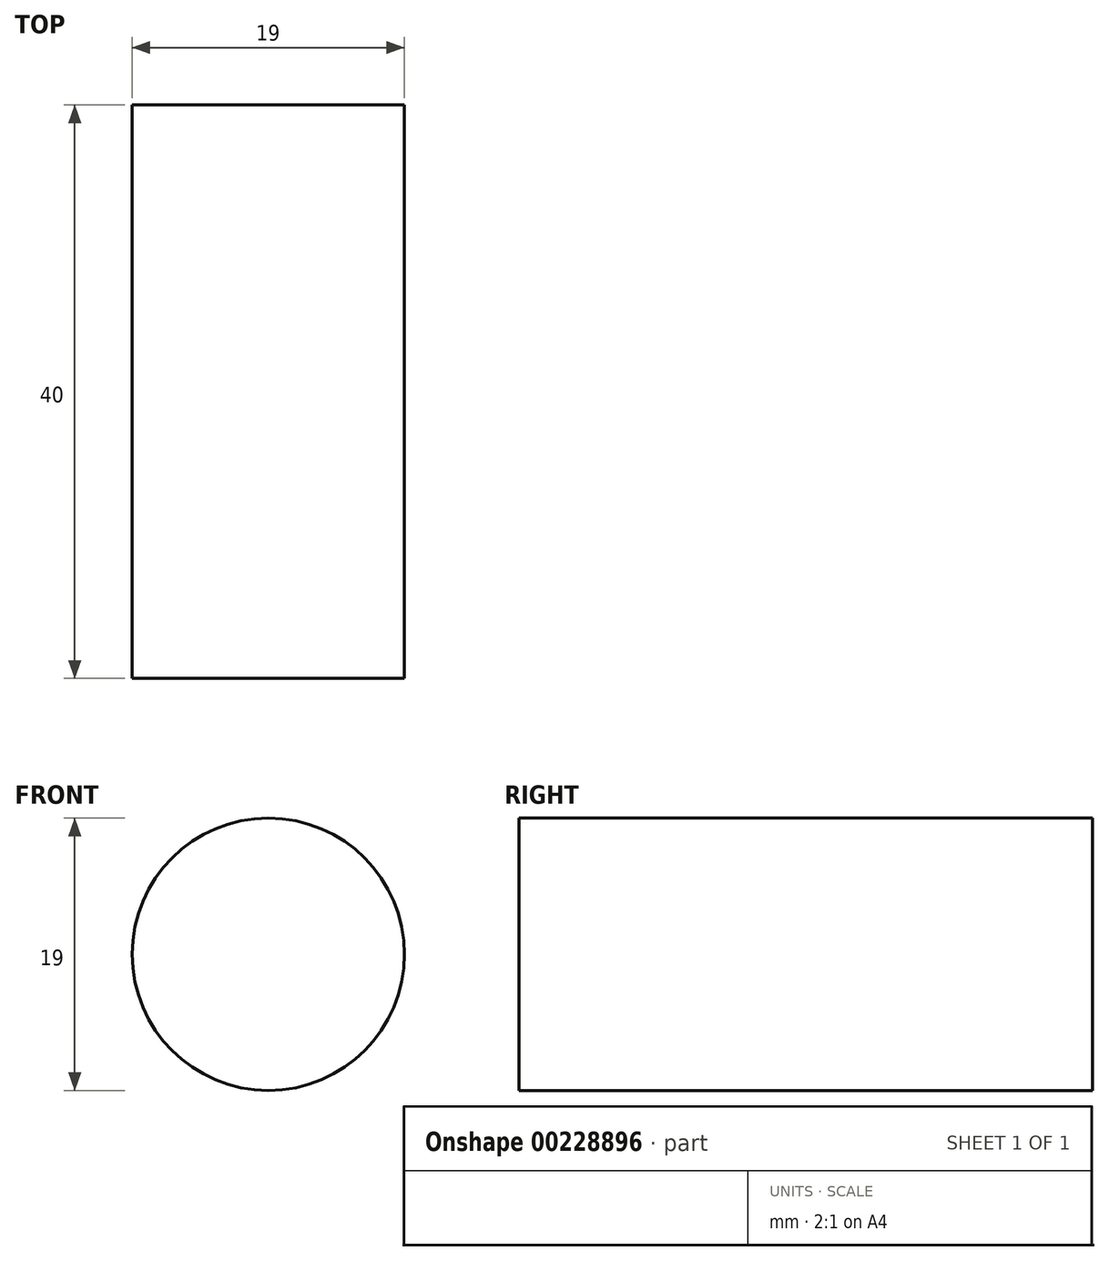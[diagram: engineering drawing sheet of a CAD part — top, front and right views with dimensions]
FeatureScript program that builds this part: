
annotation { "Feature Type Name" : "Feature", "Feature Type Description" : "" }
export const myFeature = defineFeature(function(context is Context, id is Id, definition is map)
    precondition{}
    {
        {
            var Q0;
            Q0=qCreatedBy(makeId("Top.planeOp"),FACE);
            var sketch = newSketch(context, id + "F0", { "sketchPlane" : qUnion([Q0])});
            skLineSegment(sketch, "E0.bottom", {"start": v(0, 0) * mm, "end": v(-9.5, 0) * mm});
            skLineSegment(sketch, "E0.top", {"start": v(0, 40) * mm, "end": v(-9.5, 40) * mm});
            skLineSegment(sketch, "E0.left", {"start": v(0, 0) * mm, "end": v(0, 40) * mm});
            skLineSegment(sketch, "E0.right", {"start": v(-9.5, 0) * mm, "end": v(-9.5, 40) * mm});
            skSolve(sketch);
        }
        {
            var Q0;
            Q0 = qSketchRegion(id + "F0", true);
            var Q1;
            Q1=sQuery(id+"F0.wireOp",EDGE,"E0.left");
            revolve(context, id + "F1", {"entities" : qUnion([Q0]), "axis" : qUnion([Q1]), "revolveType" : RevolveType.FULL});
        }
    });
